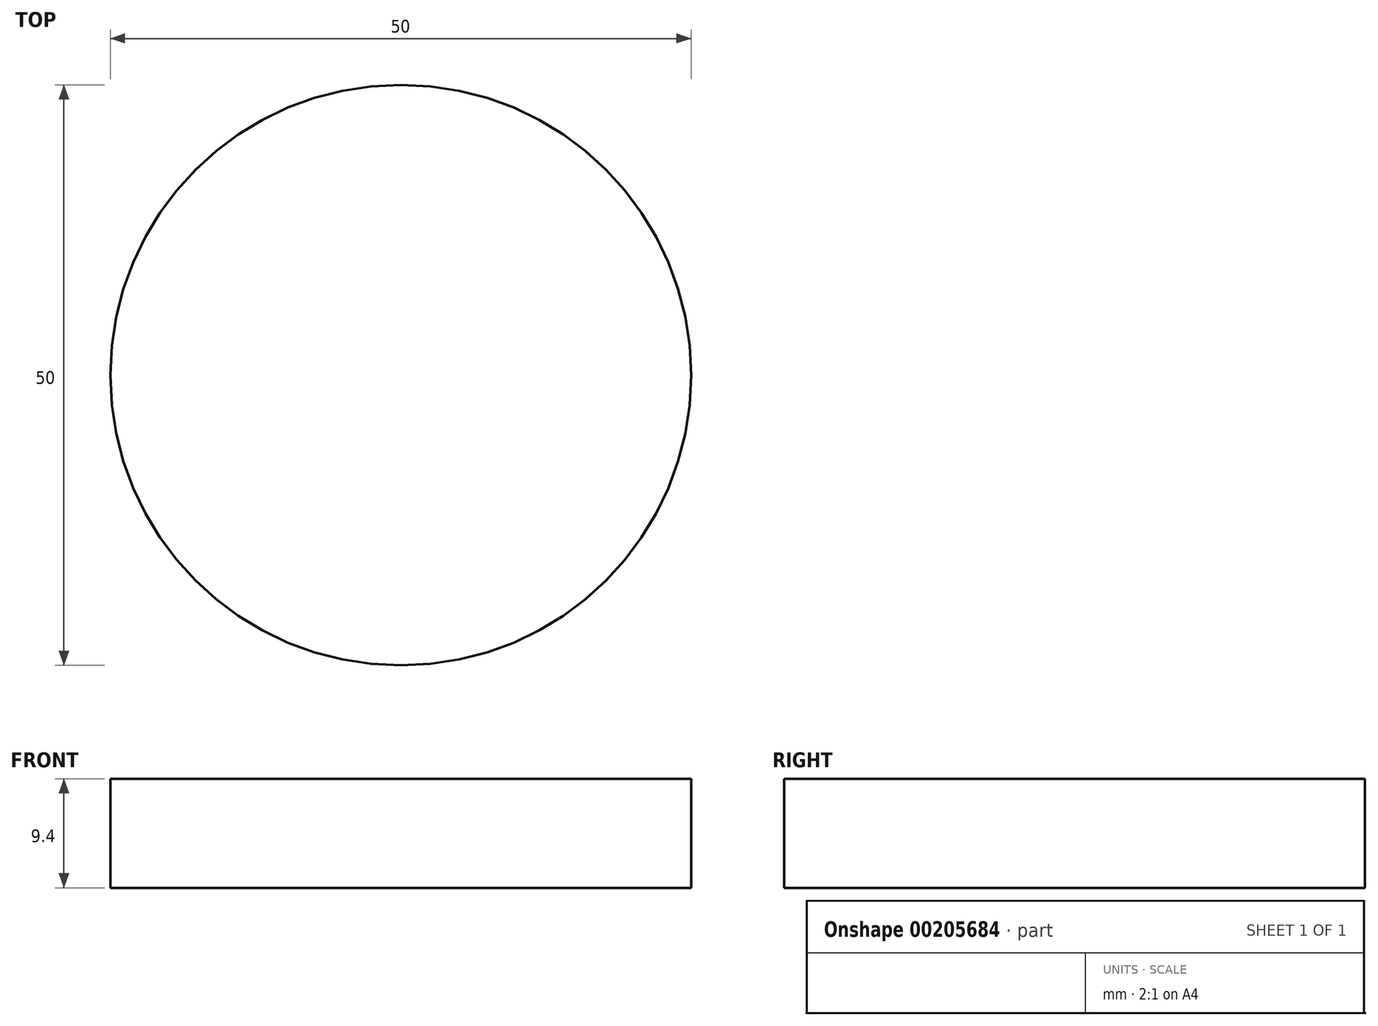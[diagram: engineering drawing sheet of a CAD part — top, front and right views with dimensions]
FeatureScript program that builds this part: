
annotation { "Feature Type Name" : "Feature", "Feature Type Description" : "" }
export const myFeature = defineFeature(function(context is Context, id is Id, definition is map)
    precondition{}
    {
        {
            var Q0;
            Q0=qCreatedBy(makeId("Top.planeOp"),FACE);
            var sketch = newSketch(context, id + "F0", { "sketchPlane" : qUnion([Q0])});
            skCircle(sketch, "E0", {"center": v(0, 0) * mm, "radius": 25 * mm});
            skSolve(sketch);
        }
        {
            var Q0;
            Q0=makeQuery(id+"F0.imprint","IMPRINT",FACE,{"disambiguationData":[TD([[makeQuery(id+"F0.imprint","IMPRINT",EDGE,{"derivedFrom":sQuery(id+"F0.wireOp",EDGE,"E0")}),1.0]])]});
            extrude(context, id + "F1", {"entities" : qUnion([Q0]), "depth" : 9.4 * mm});
        }
    });
